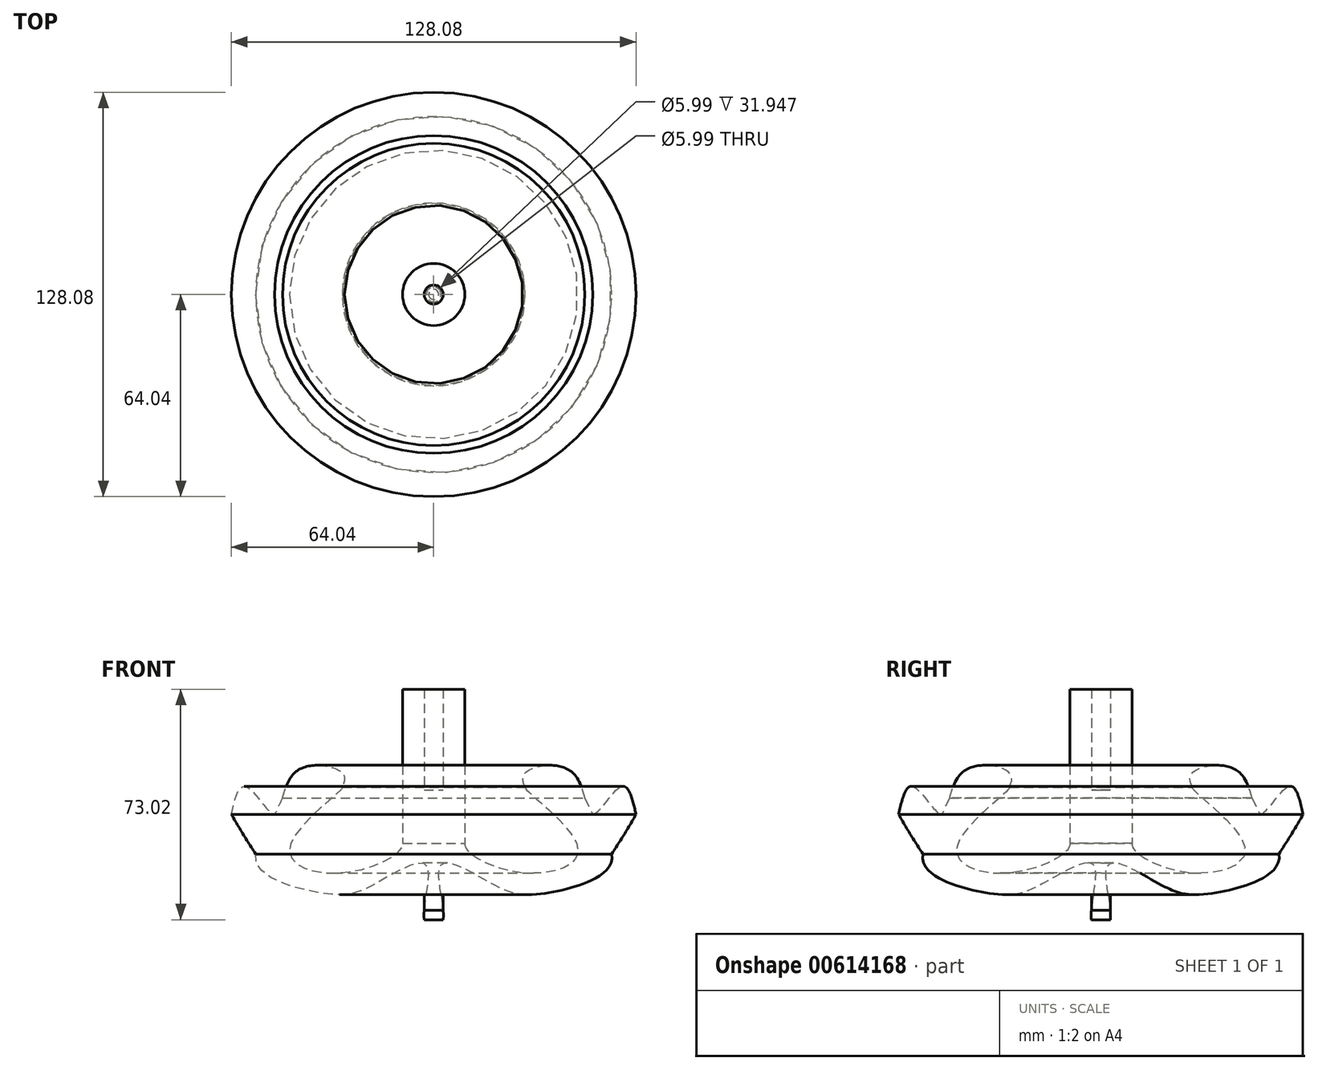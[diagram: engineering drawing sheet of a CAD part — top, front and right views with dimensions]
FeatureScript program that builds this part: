
annotation { "Feature Type Name" : "Feature", "Feature Type Description" : "" }
export const myFeature = defineFeature(function(context is Context, id is Id, definition is map)
    precondition{}
    {
        {
            var Q0;
            Q0=qCreatedBy(makeId("Front.planeOp"),FACE);
            var sketch = newSketch(context, id + "F0", { "sketchPlane" : qUnion([Q0])});
            skLineSegment(sketch, "E0", {"start": v(0, 0) * mm, "end": v(0, 7.99) * mm});
            skLineSegment(sketch, "E1", {"start": v(0, 7.99) * mm, "end": v(3, 7.99) * mm});
            skLineSegment(sketch, "E2", {"start": v(3, 7.99) * mm, "end": v(3, 0) * mm});
            skLineSegment(sketch, "E3", {"start": v(0, 7.99) * mm, "end": v(0, 41.07) * mm});
            skPoint(sketch, "E4.end.orphan", {"position": v(3, 41.07) * mm});
            skLineSegment(sketch, "E5", {"start": v(0, 41.07) * mm, "end": v(3, 41.07) * mm});
            skLineSegment(sketch, "E6", {"start": v(3, 73.02) * mm, "end": v(3, 41.07) * mm});
            skLineSegment(sketch, "E7", {"start": v(3, 73.02) * mm, "end": v(9.84, 73.02) * mm});
            skLineSegment(sketch, "E8", {"start": v(9.84, 73.02) * mm, "end": v(9.84, 24.25) * mm});
            skFitSpline(sketch, "E9", {"points": [v(3, 0) * mm, v(2.42, 17.4) * mm, v(18.97, 11.12) * mm, v(34.37, 8.27) * mm, v(56.34, 20.82) * mm, v(28.95, 41.93) * mm, v(45.5, 23.39) * mm, v(29.52, 14.83) * mm, v(9.84, 24.25) * mm], "startDerivative": vector(16.78, 134.12) * mm, "endDerivative": vector(13.99, 84.52) * mm});
            skLineSegment(sketch, "E10", {"start": v(47.86, 38.57) * mm, "end": v(50.34, 33.37) * mm});
            skFitSpline(sketch, "E11", {"points": [v(56.34, 20.82) * mm, v(60.33, 27.1) * mm, v(64.04, 33.37) * mm], "startDerivative": vector(8.07, 12.46) * mm, "endDerivative": vector(7.33, 12.65) * mm});
            skFitSpline(sketch, "E12", {"points": [v(64.04, 33.37) * mm, v(59.47, 42.22) * mm, v(50.34, 33.37) * mm, v(44.07, 46.5) * mm, v(28.95, 46.5) * mm, v(28.95, 41.93) * mm], "startDerivative": vector(-17.28, 75.69) * mm, "endDerivative": vector(14.76, -37.48) * mm});
            skFitSpline(sketch, "E13.trimOffspring", {"points": [v(64.04, 33.37) * mm, v(59.47, 42.22) * mm, v(50.34, 33.37) * mm, v(44.07, 46.5) * mm, v(28.95, 46.5) * mm, v(28.95, 41.93) * mm], "startDerivative": vector(-17.28, 75.69) * mm, "endDerivative": vector(14.76, -37.48) * mm});
            skSolve(sketch);
        }
        {
            var Q0;
            Q0 = qSketchRegion(id + "F0", true);
            var Q1;
            Q1=sQuery(id+"F0.wireOp",EDGE,"E3");
            revolve(context, id + "F1", {"entities" : qUnion([Q0]), "axis" : qUnion([Q1]), "revolveType" : RevolveType.FULL});
        }
    });
